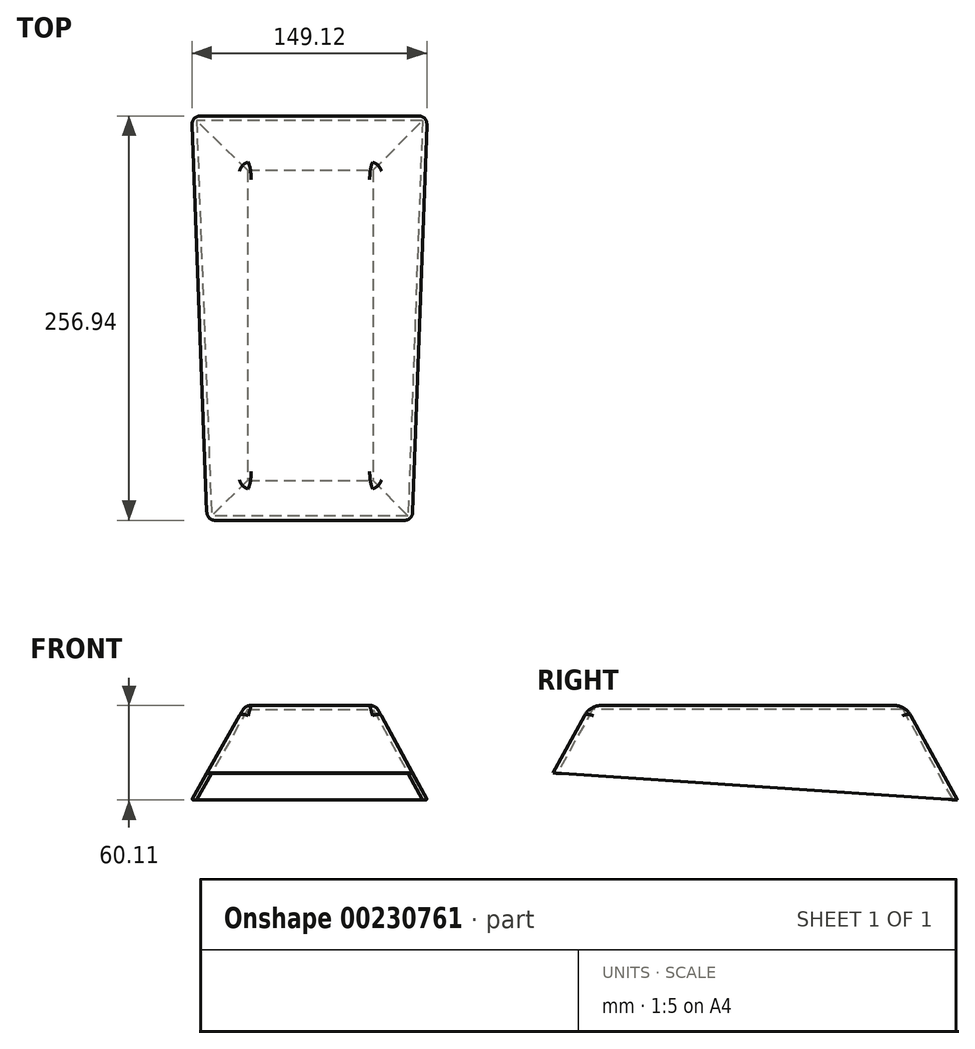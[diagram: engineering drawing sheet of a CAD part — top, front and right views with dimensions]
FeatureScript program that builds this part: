
annotation { "Feature Type Name" : "Feature", "Feature Type Description" : "" }
export const myFeature = defineFeature(function(context is Context, id is Id, definition is map)
    precondition{}
    {
        {
            var Q0;
            Q0=qCreatedBy(makeId("Top.planeOp"),FACE);
            var sketch = newSketch(context, id + "F0", { "sketchPlane" : qUnion([Q0])});
            skLineSegment(sketch, "E0.bottom", {"start": v(-45.92, 68.01) * mm, "end": v(104, 68.01) * mm});
            skLineSegment(sketch, "E0.top", {"start": v(-45.92, -200.4) * mm, "end": v(104, -200.4) * mm});
            skLineSegment(sketch, "E0.left", {"start": v(-45.92, 68.01) * mm, "end": v(-45.92, -200.4) * mm});
            skLineSegment(sketch, "E0.right", {"start": v(104, 68.01) * mm, "end": v(104, -200.4) * mm});
            skSolve(sketch);
        }
        {
            var Q0;
            Q0=makeQuery(id+"F0.imprint","IMPRINT",FACE,{"disambiguationData":[TD([[makeQuery(id+"F0.imprint","IMPRINT",EDGE,{"derivedFrom":sQuery(id+"F0.wireOp",EDGE,"E0.bottom")}),-1.0]])]});
            extrude(context, id + "F1", {"entities" : qUnion([Q0]), "depth" : 60.45 * mm});
        }
        {
            var Q0;
            Q0=makeQuery(id+"F1.opExtrude","SWEPT_FACE",FACE,{"disambiguationData":[OSD([sQuery(id+"F0.wireOp",EDGE,"E0.top")])]});
            var sketch = newSketch(context, id + "F2", { "sketchPlane" : qUnion([Q0])});
            skLineSegment(sketch, "E1", {"start": v(-45.92, 0) * mm, "end": v(-11.68, 60.45) * mm});
            skSolve(sketch);
        }
        {
            var Q0;
            {var subQ0=sQuery(id+"F2.wireOp",EDGE,"E1");Q0=makeQuery(id+"F2.imprint","IMPRINT",FACE,{"disambiguationData":[TD([[makeQuery(id+"F2.imprint","IMPRINT",EDGE,{"derivedFrom":subQ0}),1.0]])]});}
            extrude(context, id + "F3", {"entities" : qUnion([Q0]), "operationType" : NewBodyOperationType.REMOVE, "oppositeDirection" : true, "depth" : 269 * mm});
        }
        {
            var Q0;
            Q0=makeQuery(id+"F1.opExtrude","SWEPT_FACE",FACE,{"disambiguationData":[OSD([sQuery(id+"F0.wireOp",EDGE,"E0.top")])]});
            var sketch = newSketch(context, id + "F4", { "sketchPlane" : qUnion([Q0])});
            skLineSegment(sketch, "E2", {"start": v(104, 0) * mm, "end": v(71.07, 60.45) * mm});
            skSolve(sketch);
        }
        {
            var Q0;
            {var subQ0=sQuery(id+"F4.wireOp",EDGE,"E2");Q0=makeQuery(id+"F4.imprint","IMPRINT",FACE,{"disambiguationData":[TD([[makeQuery(id+"F4.imprint","IMPRINT",EDGE,{"derivedFrom":subQ0}),-1.0]])]});}
            extrude(context, id + "F5", {"entities" : qUnion([Q0]), "operationType" : NewBodyOperationType.REMOVE, "oppositeDirection" : true, "depth" : 271.53 * mm});
        }
        {
            var Q0;
            Q0=qCreatedBy(makeId("Right.planeOp"),FACE);
            var sketch = newSketch(context, id + "F6", { "sketchPlane" : qUnion([Q0])});
            skLineSegment(sketch, "E3.bottom", {"start": v(27.18, 71.99) * mm, "end": v(78.46, 71.99) * mm});
            skLineSegment(sketch, "E3.top", {"start": v(27.18, -25.37) * mm, "end": v(78.46, -25.37) * mm});
            skLineSegment(sketch, "E3.left", {"start": v(27.18, 71.99) * mm, "end": v(27.18, -25.37) * mm});
            skLineSegment(sketch, "E3.right", {"start": v(78.46, 71.99) * mm, "end": v(78.46, -25.37) * mm});
            skLineSegment(sketch, "E4", {"start": v(27.18, 71.99) * mm, "end": v(74.63, -14.28) * mm});
            skLineSegment(sketch, "E5", {"start": v(74.63, -14.28) * mm, "end": v(78.46, -25.37) * mm});
            skSolve(sketch);
        }
        {
            var Q0;
            Q0=makeQuery(id+"F6.imprint","IMPRINT",FACE,{"disambiguationData":[TD([[makeQuery(id+"F6.imprint","IMPRINT",EDGE,{"derivedFrom":sQuery(id+"F6.wireOp",EDGE,"E3.bottom")}),-1.0]])]});
            extrude(context, id + "F7", {"entities" : qUnion([Q0]), "operationType" : NewBodyOperationType.REMOVE, "oppositeDirection" : true, "depth" : 74.93 * mm, "hasSecondDirection" : true, "secondDirectionOppositeDirection" : false, "secondDirectionDepth" : 120.9 * mm});
        }
        {
            var Q0;
            Q0=qCreatedBy(makeId("Right.planeOp"),FACE);
            var sketch = newSketch(context, id + "F8", { "sketchPlane" : qUnion([Q0])});
            skLineSegment(sketch, "E6.bottom", {"start": v(-157.05, 77.75) * mm, "end": v(-215.8, 77.75) * mm});
            skLineSegment(sketch, "E6.top", {"start": v(-157.05, -28.47) * mm, "end": v(-215.8, -28.47) * mm});
            skLineSegment(sketch, "E6.left", {"start": v(-157.05, 77.75) * mm, "end": v(-157.05, -28.47) * mm});
            skLineSegment(sketch, "E6.right", {"start": v(-215.8, 77.75) * mm, "end": v(-215.8, -28.47) * mm});
            skLineSegment(sketch, "E7", {"start": v(-157.05, 77.75) * mm, "end": v(-215.8, -28.47) * mm});
            skSolve(sketch);
        }
        {
            var Q0;
            Q0=makeQuery(id+"F8.imprint","IMPRINT",FACE,{"disambiguationData":[TD([[makeQuery(id+"F8.imprint","IMPRINT",EDGE,{"derivedFrom":sQuery(id+"F8.wireOp",EDGE,"E6.bottom")}),1.0]])]});
            extrude(context, id + "F9", {"entities" : qUnion([Q0]), "operationType" : NewBodyOperationType.REMOVE, "oppositeDirection" : true, "depth" : 58.17 * mm, "hasSecondDirection" : true, "secondDirectionOppositeDirection" : false, "secondDirectionDepth" : 130.8 * mm});
        }
        {
            var Q0;
            Q0=qCreatedBy(makeId("Right.planeOp"),FACE);
            var sketch = newSketch(context, id + "F10", { "sketchPlane" : qUnion([Q0])});
            skLineSegment(sketch, "E8.bottom", {"start": v(71.73, 17.63) * mm, "end": v(-203.9, 17.63) * mm});
            skLineSegment(sketch, "E8.top", {"start": v(71.73, -24.29) * mm, "end": v(-203.9, -24.29) * mm});
            skLineSegment(sketch, "E8.left", {"start": v(71.73, 17.63) * mm, "end": v(71.73, -24.29) * mm});
            skLineSegment(sketch, "E8.right", {"start": v(-203.9, 17.63) * mm, "end": v(-203.9, -24.29) * mm});
            skLineSegment(sketch, "E9", {"start": v(71.73, 0) * mm, "end": v(-191.7, 17.63) * mm});
            skPoint(sketch, "E9.startSnap0", {"position": v(71.73, -3.33) * mm});
            skSolve(sketch);
        }
        {
            var Q0;
            {var subQ1=sQuery(id+"F10.wireOp",EDGE,"E8.top");Q0=makeQuery(id+"F10.imprint","IMPRINT",FACE,{"disambiguationData":[TD([[makeQuery(id+"F10.imprint","IMPRINT",EDGE,{"derivedFrom":subQ1}),-1.0]])]});}
            extrude(context, id + "F11", {"entities" : qUnion([Q0]), "operationType" : NewBodyOperationType.REMOVE, "oppositeDirection" : true, "depth" : 73.9 * mm, "hasSecondDirection" : true, "secondDirectionOppositeDirection" : false, "secondDirectionDepth" : 115.06 * mm});
        }
        {
            var Q0;
            Q0=makeQuery(id+"F11.boolean.opBoolean","COPY",FACE,{"derivedFrom":makeQuery(id+"F11.opExtrude","SWEPT_FACE",FACE,{"disambiguationData":[OSD([sQuery(id+"F10.wireOp",EDGE,"E9")])]})});
            shell(context, id + "F12", {"entities" : qUnion([Q0]), "thickness" : 2.54 * mm});
        }
        {
            var Q0;
            Q0=makeQuery(id+"F7.boolean.opBoolean","INTERSECT",EDGE,{"derivedFrom":[makeQuery(id+"F1.opExtrude","CAP_FACE",FACE,{"disambiguationData":[OSD([sQuery(id+"F0.wireOp",EDGE,"E0.bottom"),sQuery(id+"F0.wireOp",EDGE,"E0.top"),sQuery(id+"F0.wireOp",EDGE,"E0.left"),sQuery(id+"F0.wireOp",EDGE,"E0.right")])],"isStart":false}),makeQuery(id+"F7.opExtrude","SWEPT_FACE",FACE,{"disambiguationData":[OSD([sQuery(id+"F6.wireOp",EDGE,"E4")])]})]});
            var Q1;
            Q1=makeQuery(id+"F9.boolean.opBoolean","INTERSECT",EDGE,{"derivedFrom":[makeQuery(id+"F1.opExtrude","CAP_FACE",FACE,{"disambiguationData":[OSD([sQuery(id+"F0.wireOp",EDGE,"E0.bottom"),sQuery(id+"F0.wireOp",EDGE,"E0.top"),sQuery(id+"F0.wireOp",EDGE,"E0.left"),sQuery(id+"F0.wireOp",EDGE,"E0.right")])],"isStart":false}),makeQuery(id+"F9.opExtrude","SWEPT_FACE",FACE,{"disambiguationData":[OSD([sQuery(id+"F8.wireOp",EDGE,"E7")])]})]});
            var Q2;
            Q2=makeQuery(id+"F3.boolean.opBoolean","COPY",EDGE,{"derivedFrom":makeQuery(id+"F3.opExtrude","SWEPT_EDGE",EDGE,{"disambiguationData":[OSD([sQuery(id+"F0.wireOp",EDGE,"E0.top"),sQuery(id+"F2.wireOp",EDGE,"E1")])]})});
            var Q3;
            Q3=makeQuery(id+"F5.boolean.opBoolean","COPY",EDGE,{"derivedFrom":makeQuery(id+"F5.opExtrude","SWEPT_EDGE",EDGE,{"disambiguationData":[OSD([sQuery(id+"F0.wireOp",EDGE,"E0.top"),sQuery(id+"F4.wireOp",EDGE,"E2")])]})});
            fillet(context, id + "F13", {"entities" : qUnion([Q0, Q1, Q2, Q3]), "radius" : 12.7 * mm, "tangentPropagation" : true, "allowEdgeOverflow" : false});
        }
        {
            var Q0;
            Q0=makeQuery(id+"F7.boolean.opBoolean","INTERSECT",EDGE,{"derivedFrom":[makeQuery(id+"F3.boolean.opBoolean","COPY",FACE,{"derivedFrom":makeQuery(id+"F3.opExtrude","SWEPT_FACE",FACE,{"disambiguationData":[OSD([sQuery(id+"F2.wireOp",EDGE,"E1")])]})}),makeQuery(id+"F7.opExtrude","SWEPT_FACE",FACE,{"disambiguationData":[OSD([sQuery(id+"F6.wireOp",EDGE,"E4")])]})]});
            var Q1;
            Q1=makeQuery(id+"F7.boolean.opBoolean","INTERSECT",EDGE,{"derivedFrom":[makeQuery(id+"F5.boolean.opBoolean","COPY",FACE,{"derivedFrom":makeQuery(id+"F5.opExtrude","SWEPT_FACE",FACE,{"disambiguationData":[OSD([sQuery(id+"F4.wireOp",EDGE,"E2")])]})}),makeQuery(id+"F7.opExtrude","SWEPT_FACE",FACE,{"disambiguationData":[OSD([sQuery(id+"F6.wireOp",EDGE,"E4")])]})]});
            var Q2;
            Q2=makeQuery(id+"F9.boolean.opBoolean","INTERSECT",EDGE,{"derivedFrom":[makeQuery(id+"F3.boolean.opBoolean","COPY",FACE,{"derivedFrom":makeQuery(id+"F3.opExtrude","SWEPT_FACE",FACE,{"disambiguationData":[OSD([sQuery(id+"F2.wireOp",EDGE,"E1")])]})}),makeQuery(id+"F9.opExtrude","SWEPT_FACE",FACE,{"disambiguationData":[OSD([sQuery(id+"F8.wireOp",EDGE,"E7")])]})]});
            var Q3;
            Q3=makeQuery(id+"F9.boolean.opBoolean","INTERSECT",EDGE,{"derivedFrom":[makeQuery(id+"F5.boolean.opBoolean","COPY",FACE,{"derivedFrom":makeQuery(id+"F5.opExtrude","SWEPT_FACE",FACE,{"disambiguationData":[OSD([sQuery(id+"F4.wireOp",EDGE,"E2")])]})}),makeQuery(id+"F9.opExtrude","SWEPT_FACE",FACE,{"disambiguationData":[OSD([sQuery(id+"F8.wireOp",EDGE,"E7")])]})]});
            fillet(context, id + "F14", {"entities" : qUnion([Q0, Q1, Q2, Q3]), "radius" : 6.35 * mm, "tangentPropagation" : true, "allowEdgeOverflow" : false});
        }
    });
